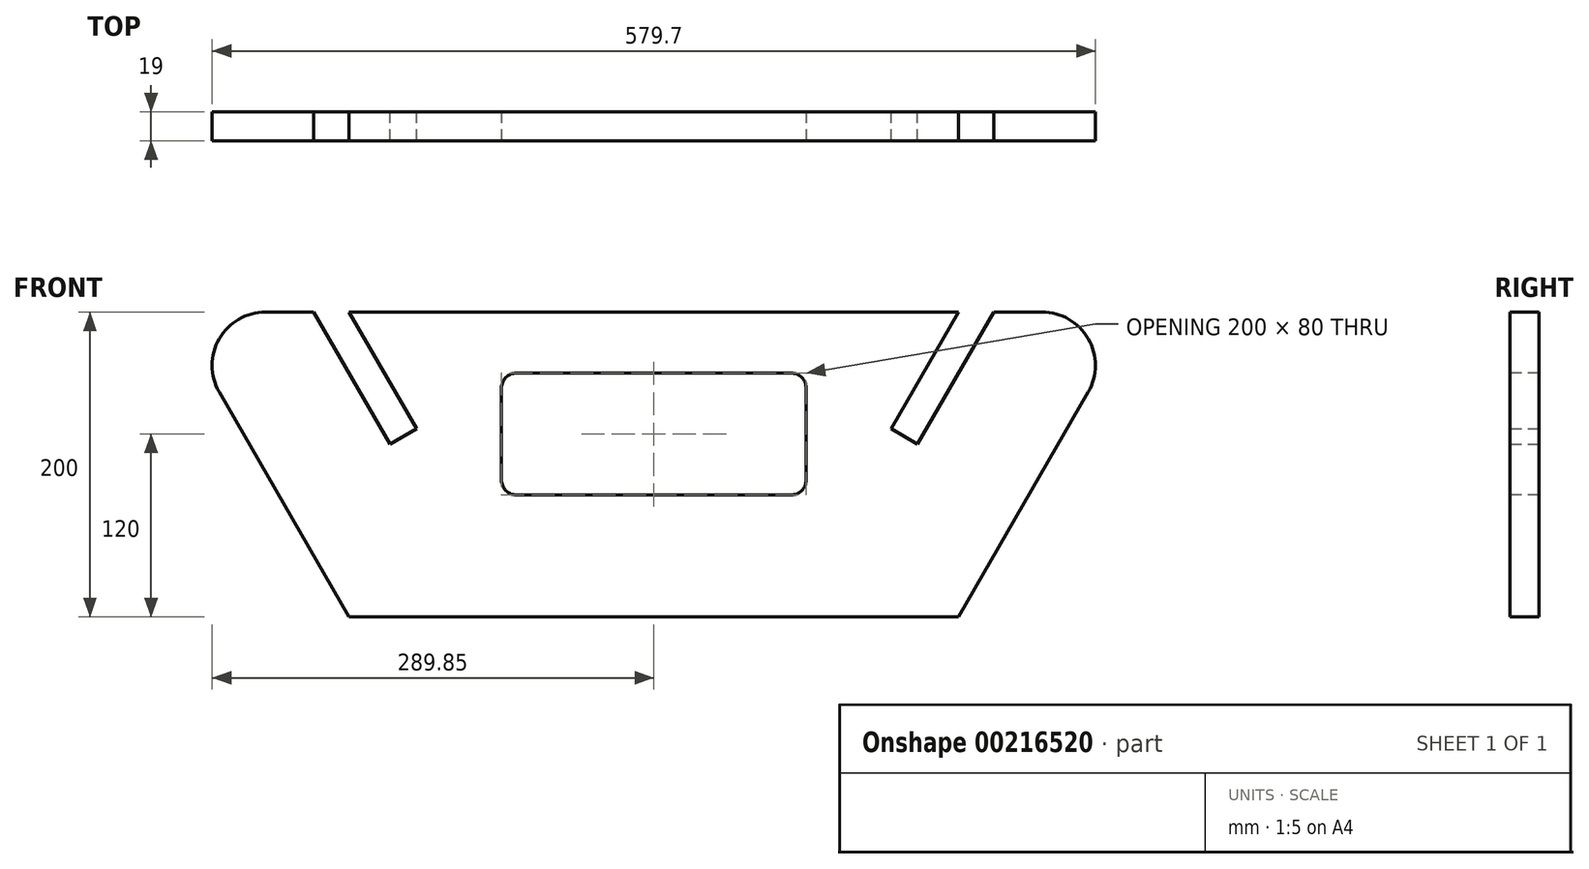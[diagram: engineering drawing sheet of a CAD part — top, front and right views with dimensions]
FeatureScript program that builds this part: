
annotation { "Feature Type Name" : "Feature", "Feature Type Description" : "" }
export const myFeature = defineFeature(function(context is Context, id is Id, definition is map)
    precondition{}
    {
        {
            var Q0;
            Q0=qCreatedBy(makeId("Front.planeOp"),FACE);
            var sketch = newSketch(context, id + "F0", { "sketchPlane" : qUnion([Q0])});
            skLineSegment(sketch, "E0", {"start": v(-200, 0) * mm, "end": v(-315.47, 200) * mm});
            skLineSegment(sketch, "E1", {"start": v(-200, 0) * mm, "end": v(200, 0) * mm});
            skLineSegment(sketch, "E2", {"start": v(315.47, 200) * mm, "end": v(223.1, 200) * mm});
            skLineSegment(sketch, "E3", {"start": v(315.47, 200) * mm, "end": v(200, 0) * mm});
            skLineSegment(sketch, "E4", {"start": v(0, 0) * mm, "end": v(0, 200) * mm, "construction": true});
            skLineSegment(sketch, "E5.top", {"start": v(-173.1, 113.4) * mm, "end": v(-155.77, 123.4) * mm});
            skLineSegment(sketch, "E5.left", {"start": v(-223.1, 200) * mm, "end": v(-173.1, 113.4) * mm});
            skLineSegment(sketch, "E5.right", {"start": v(-200, 200) * mm, "end": v(-155.77, 123.4) * mm});
            skLineSegment(sketch, "E6.MirrorCS", {"start": v(173.1, 113.4) * mm, "end": v(155.77, 123.4) * mm});
            skLineSegment(sketch, "E7.MirrorCS", {"start": v(200, 200) * mm, "end": v(155.77, 123.4) * mm});
            skLineSegment(sketch, "E8.MirrorCS", {"start": v(223.1, 200) * mm, "end": v(173.1, 113.4) * mm});
            skLineSegment(sketch, "E9.trimOffspring", {"start": v(-223.1, 200) * mm, "end": v(-315.47, 200) * mm});
            skLineSegment(sketch, "E10.trimOffspring", {"start": v(200, 200) * mm, "end": v(-200, 200) * mm});
            skSolve(sketch);
        }
        {
            var Q0;
            Q0=makeQuery(id+"F0.imprint","IMPRINT",FACE,{"disambiguationData":[TD([[makeQuery(id+"F0.imprint","IMPRINT",EDGE,{"derivedFrom":sQuery(id+"F0.wireOp",EDGE,"E0")}),-1.0]])]});
            extrude(context, id + "F1", {"entities" : qUnion([Q0]), "depth" : 19 * mm, "symmetric" : true});
        }
        {
            var Q0;
            Q0=makeQuery(id+"F1.opExtrude","CAP_FACE",FACE,{"disambiguationData":[OSD([sQuery(id+"F0.wireOp",EDGE,"E0"),sQuery(id+"F0.wireOp",EDGE,"E1"),sQuery(id+"F0.wireOp",EDGE,"E2"),sQuery(id+"F0.wireOp",EDGE,"E3"),sQuery(id+"F0.wireOp",EDGE,"E5.top"),sQuery(id+"F0.wireOp",EDGE,"E5.left"),sQuery(id+"F0.wireOp",EDGE,"E5.right"),sQuery(id+"F0.wireOp",EDGE,"E6.MirrorCS"),sQuery(id+"F0.wireOp",EDGE,"E7.MirrorCS"),sQuery(id+"F0.wireOp",EDGE,"E8.MirrorCS"),sQuery(id+"F0.wireOp",EDGE,"E9.trimOffspring"),sQuery(id+"F0.wireOp",EDGE,"E10.trimOffspring")])],"isStart":false});
            var sketch = newSketch(context, id + "F2", { "sketchPlane" : qUnion([Q0])});
            skLineSegment(sketch, "E11.bottom", {"start": v(-90, 160) * mm, "end": v(90, 160) * mm});
            skLineSegment(sketch, "E11.top", {"start": v(-90, 80) * mm, "end": v(90, 80) * mm});
            skLineSegment(sketch, "E11.left", {"start": v(-100, 150) * mm, "end": v(-100, 90) * mm});
            skLineSegment(sketch, "E11.right", {"start": v(100, 150) * mm, "end": v(100, 90) * mm});
            skLineSegment(sketch, "E12", {"start": v(0, 0) * mm, "end": v(0, 80) * mm, "construction": true});
            skPoint(sketch, "E13.visualSharp", {"position": v(-100, 160) * mm});
            skArc(sketch, "E13.filletArc", {"start": v(-90, 160) * mm, "mid": v(-97.07, 157.07) * mm, "end": v(-100, 150) * mm});
            skPoint(sketch, "E14.visualSharp", {"position": v(-100, 80) * mm});
            skArc(sketch, "E14.filletArc", {"start": v(-100, 90) * mm, "mid": v(-97.07, 82.93) * mm, "end": v(-90, 80) * mm});
            skPoint(sketch, "E15.visualSharp", {"position": v(100, 80) * mm});
            skArc(sketch, "E15.filletArc", {"start": v(90, 80) * mm, "mid": v(97.07, 82.93) * mm, "end": v(100, 90) * mm});
            skPoint(sketch, "E16.visualSharp", {"position": v(100, 160) * mm});
            skArc(sketch, "E16.filletArc", {"start": v(100, 150) * mm, "mid": v(97.07, 157.07) * mm, "end": v(90, 160) * mm});
            skSolve(sketch);
        }
        {
            var Q0;
            Q0=makeQuery(id+"F2.imprint","IMPRINT",FACE,{"disambiguationData":[TD([[makeQuery(id+"F2.imprint","IMPRINT",EDGE,{"derivedFrom":sQuery(id+"F2.wireOp",EDGE,"E11.bottom")}),-1.0]])]});
            extrude(context, id + "F3", {"entities" : qUnion([Q0]), "operationType" : NewBodyOperationType.REMOVE, "oppositeDirection" : true, "depth" : 25 * mm});
        }
        {
            var Q0;
            Q0=makeQuery(id+"F1.opExtrude","SWEPT_EDGE",EDGE,{"disambiguationData":[OSD([sQuery(id+"F0.wireOp",EDGE,"E0"),sQuery(id+"F0.wireOp",EDGE,"E9.trimOffspring")])]});
            var Q1;
            Q1=makeQuery(id+"F1.opExtrude","SWEPT_EDGE",EDGE,{"disambiguationData":[OSD([sQuery(id+"F0.wireOp",EDGE,"E2"),sQuery(id+"F0.wireOp",EDGE,"E3")])]});
            fillet(context, id + "F4", {"entities" : qUnion([Q0, Q1]), "radius" : 35 * mm, "tangentPropagation" : true, "allowEdgeOverflow" : false});
        }
    });
